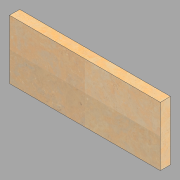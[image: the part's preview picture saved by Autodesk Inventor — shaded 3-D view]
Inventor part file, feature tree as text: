
AUTODESK INVENTOR PART (.ipt)
format: ipt  version: 2022.1 (Build 261234020, 234B)  size: 106,496 bytes
history: native  units: in
note: dims shown in document units (in); Inventor stores cm internally (conversion verified against a paired STEP export)
features: extrude x1, sketch x1
ambient origin geometry x8: Origin, YZ Plane, XZ Plane, XY Plane, X Axis, Y Axis, Z Axis, Center Point
bodies: Solid1 (feature_tree)
feature tree (2):
  extrude  "Extrusion1"  Depth=11.625in
  sketch  "Sketch1"  dims[d0=29.625in d1=11.625in d2=2.0in d3=0.0in]
